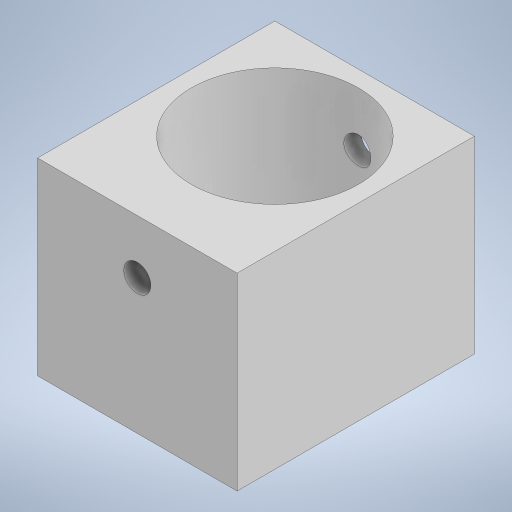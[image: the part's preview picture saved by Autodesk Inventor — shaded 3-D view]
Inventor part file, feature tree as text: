
AUTODESK INVENTOR PART (.ipt)
format: ipt  version: 2023.5 (Build 275446000, 446)  size: 246,784 bytes
history: native  units: in
note: dims shown in document units (in); Inventor stores cm internally (conversion verified against a paired STEP export)
features: extrude x6, sketch x4
ambient origin geometry x8: Origin, YZ Plane, XZ Plane, XY Plane, X Axis, Y Axis, Z Axis, Center Point
bodies: Solid1 (feature_tree)
feature tree (10):
  extrude  "Extrusion1"  Depth=1.4567in
  extrude  "Extrusion2"  Depth=0.7283in
  extrude  "Extrusion3"  Depth=1.378in TaperAngle=0.0deg
  extrude  "Extrusion4"  Depth=0.1969in TaperAngle=0.0deg
  extrude  "Extrusion5"  Depth=0.1969in
  extrude  "Extrusion6"  Depth=0.1969in TaperAngle=0.0deg
  sketch  "Sketch3"  dims[d0=1.4567in d1=1.4567in]
  sketch  "Sketch5"  dims[d2=0.7283in d3=0.7283in]
  sketch  "Sketch6"  dims[d4=1.2205in d5=1.378in d6=0.0in]
  sketch  "Sketch7"  dims[d8=0.3543in d9=0.1969in d10=0.0in d11=0.1969in d12=0.1969in d13=0.0in d14=0.0787in d15=0.0in d16=0.1969in d17=0.0in d18=0.7283in d19=0.7283in d22=0.3937in d24=0.1969in d25=0.3937in d26=0.7283in d27=0.0in d28=0.0in d21=0.0197in d23=0.0197in]
